# Revit family: BL726LEDHT - 2015
name_source: partatom
category: Lighting Fixtures
revit_build: Autodesk Revit LT 2017 (Build: 20160225_1515(x64)
units: mm (PartAtom-declared; Revit-internal decimal feet)

## family parameters
Cut with Voids When Loaded = No
Host = Face
Light Source = Yes
Part Type = Normal
Room Calculation Point = No
Round Connector Dimension = Use Diameter
Shared = No

## types (6) — shared parameters
Color Filter = 16777215
Default Elevation = 4' - 0"
Description = BOXLED High-Bay Luminaires for Commercial
and Industrial applications.
Dimming Lamp Color Temperature Shift = <None>
Emit from Line Length = 2' - 0"
Lamp = LED
Manufacturer = BEGHELLI
Model = BOX LED
Tilt Angle = -90.00°
Type Comments = The BOXLED is ideal for damp or wet applications
including warehouses, factories, gymnasiums, loading docks, logistic
centers and open ceiling environments.
Type Image = <None>

## per-type parameters (varying)
| type | Photometric Web File | Wattage Comments |
| BL736LEDHTHOWT40ASY120-277V | BL726LEDHTHOASYWT40120-277V TO REVIT.ies | 90W |
| BL736LEDHTHOWT40120-277V | BL726LEDHTHOWT40120-277V TO REVIT.ies | 90W |
| BL736LEDHTLOWT40120-277V | BL726LEDHTLOWT40120-277V TO REVIT.ies | 50W |
| BL736LEDHTLOWT40ASY120-277V | BL726LEDHTLOASYWT40120-277V TO REVIT.ies | 50W |
| BL736LEDHTMOWT40ASY120-277V | BL726LEDHTMOASYWT40120-277V TO REVIT.ies | 70W |
| BL736LEDHTMOWT40120-277V | BL726LEDHTMOWT40120-277V TO REVIT.ies | 70W |

## geometry (parser evidence)
native form markers: Sweep x17
no freeform markers — native parametric forms only
